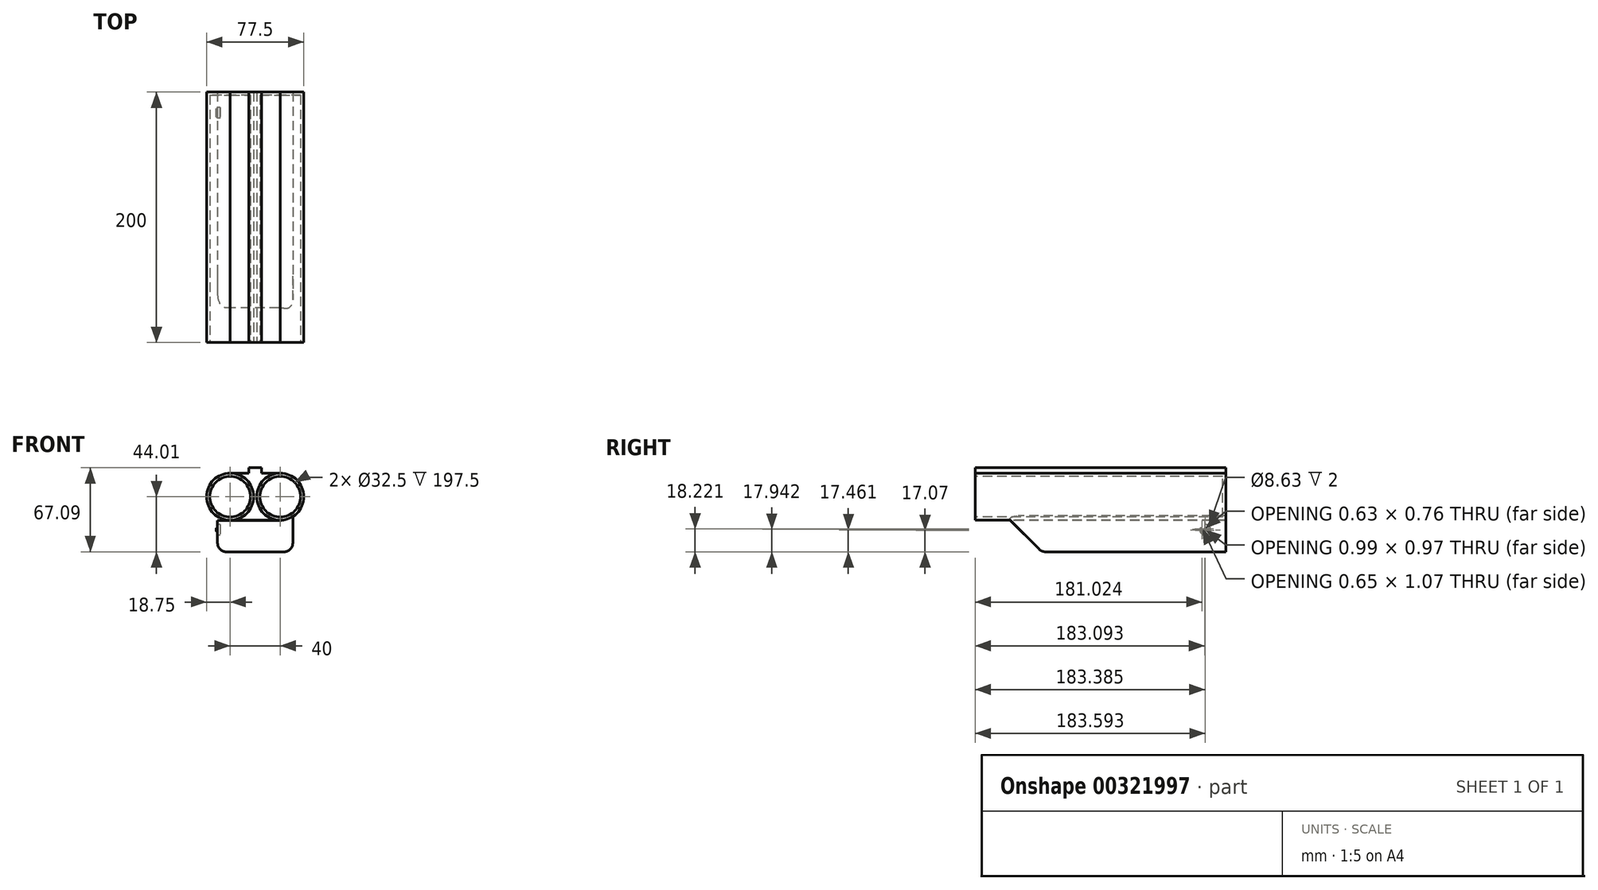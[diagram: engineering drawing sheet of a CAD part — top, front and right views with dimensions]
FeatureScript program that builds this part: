
annotation { "Feature Type Name" : "Feature", "Feature Type Description" : "" }
export const myFeature = defineFeature(function(context is Context, id is Id, definition is map)
    precondition{}
    {
        {
            var Q0;
            Q0=qCreatedBy(makeId("Front.planeOp"),FACE);
            var sketch = newSketch(context, id + "F0", { "sketchPlane" : qUnion([Q0])});
            skLineSegment(sketch, "E0", {"start": v(-20, 0) * mm, "end": v(20, 0) * mm});
            skCircle(sketch, "E1", {"center": v(-20, 0) * mm, "radius": 18.75 * mm});
            skCircle(sketch, "E2", {"center": v(20, 0) * mm, "radius": 18.75 * mm});
            skSolve(sketch);
        }
        {
            var Q0;
            Q0=makeQuery(id+"F0.imprint","IMPRINT",FACE,{"disambiguationData":[TD([[makeQuery(id+"F0.imprint","IMPRINT",EDGE,{"derivedFrom":sQuery(id+"F0.wireOp",EDGE,"E1")}),1.0]])]});
            var Q1;
            Q1=makeQuery(id+"F0.imprint","IMPRINT",FACE,{"disambiguationData":[TD([[makeQuery(id+"F0.imprint","IMPRINT",EDGE,{"derivedFrom":sQuery(id+"F0.wireOp",EDGE,"E2")}),1.0]])]});
            extrude(context, id + "F1", {"entities" : qUnion([Q0, Q1]), "oppositeDirection" : true, "depth" : 200 * mm});
        }
        {
            var Q0;
            Q0=qCreatedBy(makeId("Front.planeOp"),FACE);
            var sketch = newSketch(context, id + "F2", { "sketchPlane" : qUnion([Q0])});
            skLineSegment(sketch, "E3.bottom", {"start": v(-5, 18.75) * mm, "end": v(5, 18.75) * mm});
            skLineSegment(sketch, "E3.top", {"start": v(-5, -18.75) * mm, "end": v(5, -18.75) * mm});
            skPoint(sketch, "E3.middle", {"position": v(0, 0) * mm});
            skLineSegment(sketch, "E4", {"start": v(5, -18.75) * mm, "end": v(20, -18.75) * mm});
            skLineSegment(sketch, "E5", {"start": v(-5, -18.75) * mm, "end": v(-20, -18.75) * mm});
            skLineSegment(sketch, "E6", {"start": v(5, 18.75) * mm, "end": v(20, 18.75) * mm});
            skLineSegment(sketch, "E7", {"start": v(-5, 18.75) * mm, "end": v(-20, 18.75) * mm});
            skLineSegment(sketch, "E8", {"start": v(0, 18.75) * mm, "end": v(0, -18.75) * mm, "construction": true});
            skLineSegment(sketch, "E9", {"start": v(-20, 0) * mm, "end": v(20, 0) * mm, "construction": true});
            skLineSegment(sketch, "E10", {"start": v(-5, 18.75) * mm, "end": v(-5, 23.08) * mm});
            skLineSegment(sketch, "E11", {"start": v(-5, 23.08) * mm, "end": v(5, 23.08) * mm});
            skLineSegment(sketch, "E12", {"start": v(5, 23.08) * mm, "end": v(5, 18.75) * mm});
            skArc(sketch, "E13", {"start": v(-20, 18.75) * mm, "mid": v(-1.25, 0) * mm, "end": v(-20, -18.75) * mm});
            skArc(sketch, "E14", {"start": v(20, 18.75) * mm, "mid": v(1.25, 0) * mm, "end": v(20, -18.75) * mm});
            skSolve(sketch);
        }
        {
            var Q0;
            {var subQ0=sQuery(id+"F2.wireOp",EDGE,"E7");Q0=makeQuery(id+"F2.imprint","IMPRINT",FACE,{"disambiguationData":[TD([[makeQuery(id+"F2.imprint","IMPRINT",EDGE,{"derivedFrom":subQ0}),1.0]])]});}
            var Q1;
            {var subQ3=sQuery(id+"F2.wireOp",EDGE,"E3.bottom");Q1=makeQuery(id+"F2.imprint","IMPRINT",FACE,{"disambiguationData":[TD([[makeQuery(id+"F2.imprint","IMPRINT",EDGE,{"derivedFrom":subQ3}),-1.0]])]});}
            var Q2;
            {var subQ0=sQuery(id+"F2.wireOp",EDGE,"E6");Q2=makeQuery(id+"F2.imprint","IMPRINT",FACE,{"disambiguationData":[TD([[makeQuery(id+"F2.imprint","IMPRINT",EDGE,{"derivedFrom":subQ0}),-1.0]])]});}
            var Q3;
            {var subQ0=sQuery(id+"F2.wireOp",EDGE,"E4");Q3=makeQuery(id+"F2.imprint","IMPRINT",FACE,{"disambiguationData":[TD([[makeQuery(id+"F2.imprint","IMPRINT",EDGE,{"derivedFrom":subQ0}),1.0]])]});}
            var Q4;
            {var subQ0=sQuery(id+"F2.wireOp",EDGE,"E5");Q4=makeQuery(id+"F2.imprint","IMPRINT",FACE,{"disambiguationData":[TD([[makeQuery(id+"F2.imprint","IMPRINT",EDGE,{"derivedFrom":subQ0}),-1.0]])]});}
            var Q5;
            Q5=makeQuery(id+"F2.imprint","IMPRINT",FACE,{"disambiguationData":[TD([[makeQuery(id+"F2.imprint","IMPRINT",EDGE,{"derivedFrom":sQuery(id+"F2.wireOp",EDGE,"E3.bottom")}),1.0]])]});
            extrude(context, id + "F3", {"entities" : qUnion([Q0, Q1, Q2, Q3, Q4, Q5]), "oppositeDirection" : true, "depth" : 200 * mm});
        }
        {
            var Q0;
            Q0=makeQuery(id+"F1.opExtrude","CAP_FACE",FACE,{"disambiguationData":[OSD([sQuery(id+"F0.wireOp",EDGE,"E1")])],"isStart":true});
            var Q1;
            Q1=makeQuery(id+"F1.opExtrude","CAP_FACE",FACE,{"disambiguationData":[OSD([sQuery(id+"F0.wireOp",EDGE,"E2")])],"isStart":true});
            shell(context, id + "F4", {"entities" : qUnion([Q0, Q1]), "thickness" : 2.5 * mm});
        }
        {
            var Q0;
            Q0=qCreatedBy(makeId("Front.planeOp"),FACE);
            cPlane(context, id + "F5", {"entities" : qUnion([Q0]), "cplaneType" : CPlaneType.OFFSET, "offset" : 25 * mm, "oppositeDirection" : true, "width" : 150 * mm, "height" : 150 * mm});
        }
        {
            var Q0;
            Q0=qCreatedBy(id+"F5.planeOp",FACE);
            var sketch = newSketch(context, id + "F6", { "sketchPlane" : qUnion([Q0])});
            skLineSegment(sketch, "E15.bottom", {"start": v(30, -19.01) * mm, "end": v(-30, -19.01) * mm});
            skLineSegment(sketch, "E15.top", {"start": v(30, -44.01) * mm, "end": v(-30, -44.01) * mm});
            skLineSegment(sketch, "E15.left", {"start": v(30, -19.01) * mm, "end": v(30, -44.01) * mm});
            skLineSegment(sketch, "E15.right", {"start": v(-30, -19.01) * mm, "end": v(-30, -44.01) * mm});
            skPoint(sketch, "E15.middle", {"position": v(0, -31.51) * mm});
            skLineSegment(sketch, "E16", {"start": v(0, 0) * mm, "end": v(-18.75, 0) * mm, "construction": true});
            skLineSegment(sketch, "E17", {"start": v(0, 23.68) * mm, "end": v(0, -19.01) * mm, "construction": true});
            skArc(sketch, "E18", {"start": v(-18.75, -19.01) * mm, "mid": v(-24.67, -18.07) * mm, "end": v(-30, -15.33) * mm});
            skLineSegment(sketch, "E19", {"start": v(-30, -15.33) * mm, "end": v(-30, -19.01) * mm});
            skLineSegment(sketch, "E20.MirrorCS", {"start": v(30, -15.33) * mm, "end": v(30, -19.01) * mm});
            skArc(sketch, "E21.MirrorCS", {"start": v(18.75, -19.01) * mm, "mid": v(24.67, -18.07) * mm, "end": v(30, -15.33) * mm});
            skLineSegment(sketch, "E22.MirrorCS", {"start": v(0, 0) * mm, "end": v(18.75, 0) * mm, "construction": true});
            skSolve(sketch);
        }
        {
            var Q0;
            Q0=makeQuery(id+"F6.imprint","IMPRINT",FACE,{"disambiguationData":[TD([[makeQuery(id+"F6.imprint","IMPRINT",EDGE,{"derivedFrom":sQuery(id+"F6.wireOp",EDGE,"E15.bottom")}),1.0]])]});
            var Q1;
            {var subQ2=sQuery(id+"F6.wireOp",EDGE,"E18");Q1=makeQuery(id+"F6.imprint","IMPRINT",FACE,{"disambiguationData":[TD([[makeQuery(id+"F6.imprint","IMPRINT",EDGE,{"derivedFrom":subQ2}),1.0]])]});}
            var Q2;
            {var subQ0=sQuery(id+"F6.wireOp",EDGE,"E20.MirrorCS");Q2=makeQuery(id+"F6.imprint","IMPRINT",FACE,{"disambiguationData":[TD([[makeQuery(id+"F6.imprint","IMPRINT",EDGE,{"derivedFrom":subQ0}),-1.0]])]});}
            extrude(context, id + "F7", {"entities" : qUnion([Q0, Q1, Q2]), "oppositeDirection" : true, "depth" : 175 * mm});
        }
        {
            var Q0;
            Q0=makeQuery(id+"F7.opExtrude","CAP_EDGE",EDGE,{"disambiguationData":[OSD([sQuery(id+"F6.wireOp",EDGE,"E15.top")])],"isStart":true});
            chamfer(context, id + "F8", {"entities" : qUnion([Q0]), "width" : 28 * mm, "tangentPropagation" : true});
        }
        {
            var Q0;
            {var subQ0=sQuery(id+"F6.wireOp",EDGE,"E15.top");Q0=makeQuery(id+"F8.opChamfer","BLEND_EDGE",EDGE,{"blendedFrom":[makeQuery(id+"F7.opExtrude","CAP_EDGE",EDGE,{"disambiguationData":[OSD([subQ0])],"isStart":true}),makeQuery(id+"F7.opExtrude","SWEPT_FACE",FACE,{"disambiguationData":[OSD([subQ0])]})],"blendedInto":[makeQuery(id+"F7.opExtrude","SWEPT_FACE",FACE,{"disambiguationData":[OSD([subQ0])]})]});}
            var Q1;
            Q1=makeQuery(id+"F7.opExtrude","SWEPT_EDGE",EDGE,{"disambiguationData":[OSD([sQuery(id+"F6.wireOp",EDGE,"E15.top"),sQuery(id+"F6.wireOp",EDGE,"E15.right")])]});
            var Q2;
            Q2=makeQuery(id+"F8.opChamfer","BLEND_EDGE",EDGE,{"blendedFrom":[makeQuery(id+"F7.opExtrude","CAP_EDGE",EDGE,{"disambiguationData":[OSD([sQuery(id+"F6.wireOp",EDGE,"E15.top")])],"isStart":true}),makeQuery(id+"F7.opExtrude","SWEPT_FACE",FACE,{"disambiguationData":[OSD([sQuery(id+"F6.wireOp",EDGE,"E15.right"),sQuery(id+"F6.wireOp",EDGE,"E19")])]})],"blendedInto":[makeQuery(id+"F7.opExtrude","SWEPT_FACE",FACE,{"disambiguationData":[OSD([sQuery(id+"F6.wireOp",EDGE,"E15.right"),sQuery(id+"F6.wireOp",EDGE,"E19")])]})]});
            var Q3;
            Q3=makeQuery(id+"F8.opChamfer","BLEND_EDGE",EDGE,{"blendedFrom":[makeQuery(id+"F7.opExtrude","CAP_EDGE",EDGE,{"disambiguationData":[OSD([sQuery(id+"F6.wireOp",EDGE,"E15.top")])],"isStart":true}),makeQuery(id+"F7.opExtrude","SWEPT_FACE",FACE,{"disambiguationData":[OSD([sQuery(id+"F6.wireOp",EDGE,"E15.left"),sQuery(id+"F6.wireOp",EDGE,"E20.MirrorCS")])]})],"blendedInto":[makeQuery(id+"F7.opExtrude","SWEPT_FACE",FACE,{"disambiguationData":[OSD([sQuery(id+"F6.wireOp",EDGE,"E15.left"),sQuery(id+"F6.wireOp",EDGE,"E20.MirrorCS")])]})]});
            var Q4;
            Q4=makeQuery(id+"F7.opExtrude","SWEPT_EDGE",EDGE,{"disambiguationData":[OSD([sQuery(id+"F6.wireOp",EDGE,"E15.top"),sQuery(id+"F6.wireOp",EDGE,"E15.left")])]});
            fillet(context, id + "F9", {"entities" : qUnion([Q0, Q1, Q2, Q3, Q4]), "radius" : 7 * mm, "tangentPropagation" : true, "allowEdgeOverflow" : false});
        }
        {
            var Q0;
            Q0=makeQuery(id+"F7.opExtrude","SWEPT_FACE",FACE,{"disambiguationData":[OSD([sQuery(id+"F6.wireOp",EDGE,"E15.right"),sQuery(id+"F6.wireOp",EDGE,"E19")])]});
            var sketch = newSketch(context, id + "F10", { "sketchPlane" : qUnion([Q0])});
            skCircle(sketch, "E23", {"center": v(-183.6, -26.55) * mm, "radius": 4.31 * mm});
            skSolve(sketch);
        }
        {
            var Q0;
            Q0=makeQuery(id+"F10.imprint","IMPRINT",FACE,{"disambiguationData":[TD([[makeQuery(id+"F10.imprint","IMPRINT",EDGE,{"derivedFrom":sQuery(id+"F10.wireOp",EDGE,"E23")}),1.0]])]});
            var Q1;
            Q1=makeQuery(id+"F10.imprint","IMPRINT",FACE,{"disambiguationData":[TD([[makeQuery(id+"F10.imprint","IMPRINT",EDGE,{"derivedFrom":sQuery(id+"F10.wireOp",EDGE,"X7ge5MwT-96gP-UAvd-bBBt-mfo7WaEUFz7F")}),-1.0]])]});
            var Q2;
            Q2=makeQuery(id+"F10.imprint","IMPRINT",FACE,{"disambiguationData":[TD([[makeQuery(id+"F10.imprint","IMPRINT",EDGE,{"derivedFrom":sQuery(id+"F10.wireOp",EDGE,"iHbuA6NF-MX3I-d9Ea-5ZIp-ToZ3T7Jsef1d")}),1.0]])]});
            extrude(context, id + "F11", {"entities" : qUnion([Q0, Q1, Q2]), "operationType" : NewBodyOperationType.REMOVE, "oppositeDirection" : true, "depth" : 2 * mm});
        }
        {
            var Q0;
            Q0=makeQuery(id+"F7.opExtrude","SWEPT_FACE",FACE,{"disambiguationData":[OSD([sQuery(id+"F6.wireOp",EDGE,"E15.right"),sQuery(id+"F6.wireOp",EDGE,"E19")])]});
            var sketch = newSketch(context, id + "F12", { "sketchPlane" : qUnion([Q0])});
            skText(sketch, "E24", { "text": "M&A", "fontName": "OpenSans-Italic.ttf"});
            const initialGuessF12  = {"E24": [-0.18707, -0.02762, 1, 0, 0.00242]};
            skSetInitialGuess(sketch, initialGuessF12);
            skSolve(sketch);
        }
        {
            var Q0;
            Q0 = qSketchRegion(id + "F12", true);
            extrude(context, id + "F13", {"entities" : qUnion([Q0]), "depth" : 1 * mm});
        }
    });
